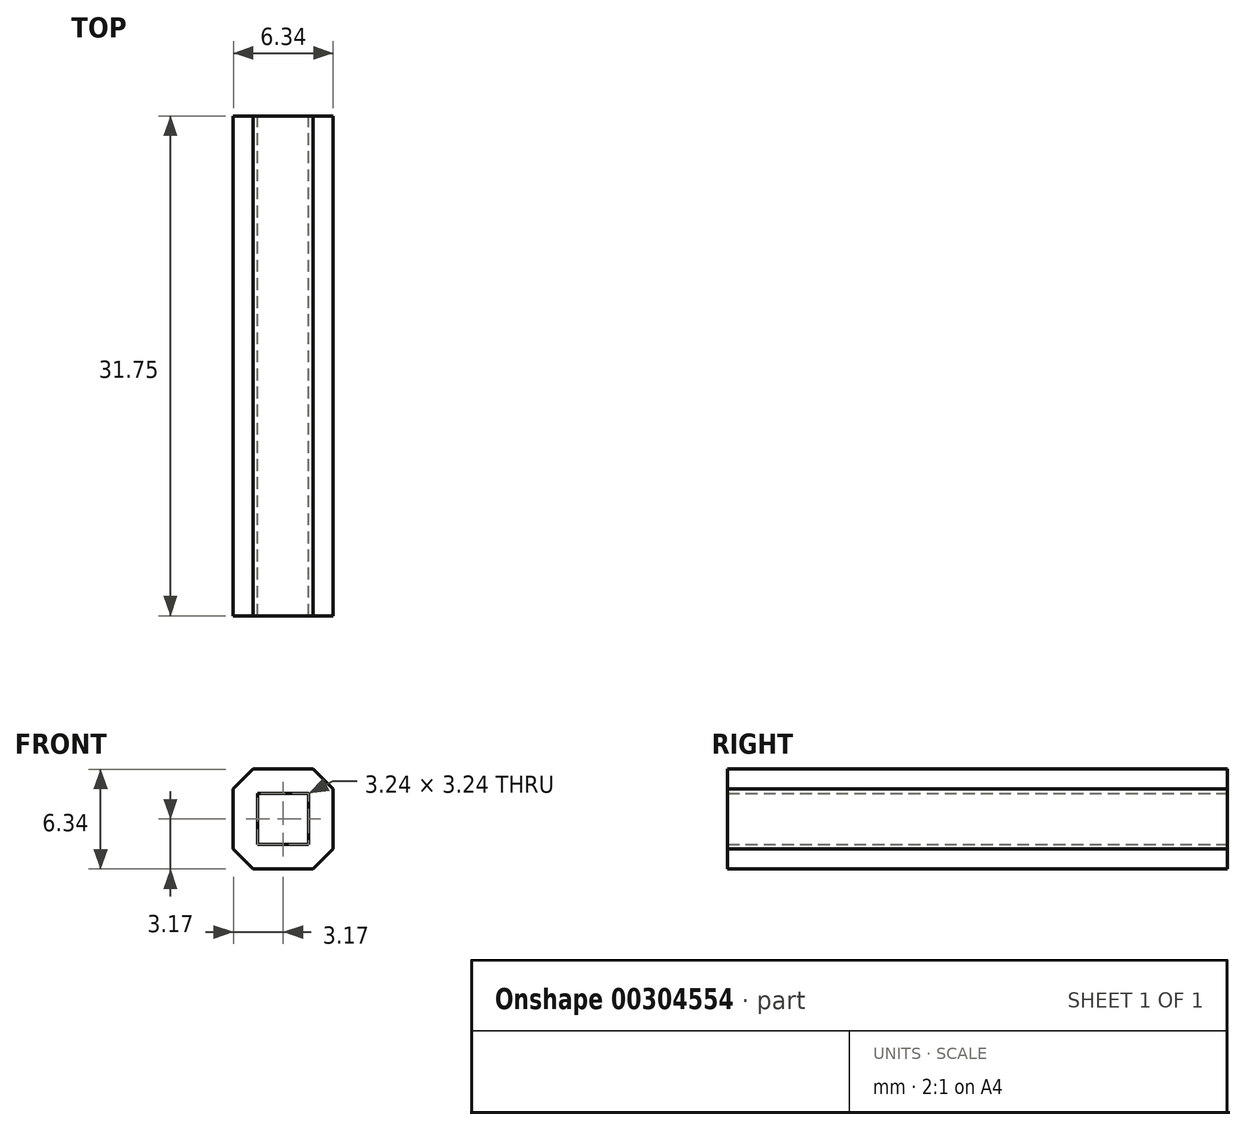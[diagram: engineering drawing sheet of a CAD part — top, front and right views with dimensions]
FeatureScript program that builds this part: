
annotation { "Feature Type Name" : "Feature", "Feature Type Description" : "" }
export const myFeature = defineFeature(function(context is Context, id is Id, definition is map)
    precondition{}
    {
        {
            var Q0;
            Q0=qCreatedBy(makeId("Front.planeOp"),FACE);
            var sketch = newSketch(context, id + "F0", { "sketchPlane" : qUnion([Q0])});
            skLineSegment(sketch, "E0.bottom", {"start": v(1.62, 1.62) * mm, "end": v(-1.62, 1.62) * mm});
            skLineSegment(sketch, "E0.top", {"start": v(1.62, -1.62) * mm, "end": v(-1.62, -1.62) * mm});
            skLineSegment(sketch, "E0.left", {"start": v(1.62, 1.62) * mm, "end": v(1.62, -1.62) * mm});
            skLineSegment(sketch, "E0.right", {"start": v(-1.62, 1.62) * mm, "end": v(-1.62, -1.62) * mm});
            skPoint(sketch, "E0.middle", {"position": v(0, 0) * mm});
            skLineSegment(sketch, "E1.bottom", {"start": v(3.17, 3.18) * mm, "end": v(-3.18, 3.17) * mm});
            skLineSegment(sketch, "E1.top", {"start": v(3.18, -3.17) * mm, "end": v(-3.17, -3.18) * mm});
            skLineSegment(sketch, "E1.left", {"start": v(3.18, 3.18) * mm, "end": v(3.18, -3.17) * mm});
            skLineSegment(sketch, "E1.right", {"start": v(-3.18, 3.17) * mm, "end": v(-3.18, -3.18) * mm});
            skSolve(sketch);
        }
        {
            var Q0;
            Q0=makeQuery(id+"F0.imprint","IMPRINT",FACE,{"disambiguationData":[TD([[makeQuery(id+"F0.imprint","IMPRINT",EDGE,{"derivedFrom":sQuery(id+"F0.wireOp",EDGE,"E0.bottom")}),-1.0]])]});
            extrude(context, id + "F1", {"entities" : qUnion([Q0]), "depth" : 31.75 * mm});
        }
        {
            var Q0;
            Q0=makeQuery(id+"F1.opExtrude","SWEPT_EDGE",EDGE,{"disambiguationData":[OSD([sQuery(id+"F0.wireOp",EDGE,"E1.bottom"),sQuery(id+"F0.wireOp",EDGE,"E1.left")])]});
            var Q1;
            Q1=makeQuery(id+"F1.opExtrude","SWEPT_EDGE",EDGE,{"disambiguationData":[OSD([sQuery(id+"F0.wireOp",EDGE,"E1.top"),sQuery(id+"F0.wireOp",EDGE,"E1.left")])]});
            var Q2;
            Q2=makeQuery(id+"F1.opExtrude","SWEPT_EDGE",EDGE,{"disambiguationData":[OSD([sQuery(id+"F0.wireOp",EDGE,"E1.top"),sQuery(id+"F0.wireOp",EDGE,"E1.right")])]});
            var Q3;
            Q3=makeQuery(id+"F1.opExtrude","SWEPT_EDGE",EDGE,{"disambiguationData":[OSD([sQuery(id+"F0.wireOp",EDGE,"E1.bottom"),sQuery(id+"F0.wireOp",EDGE,"E1.right")])]});
            chamfer(context, id + "F2", {"entities" : qUnion([Q0, Q1, Q2, Q3]), "width" : 1.27 * mm, "tangentPropagation" : true});
        }
    });
